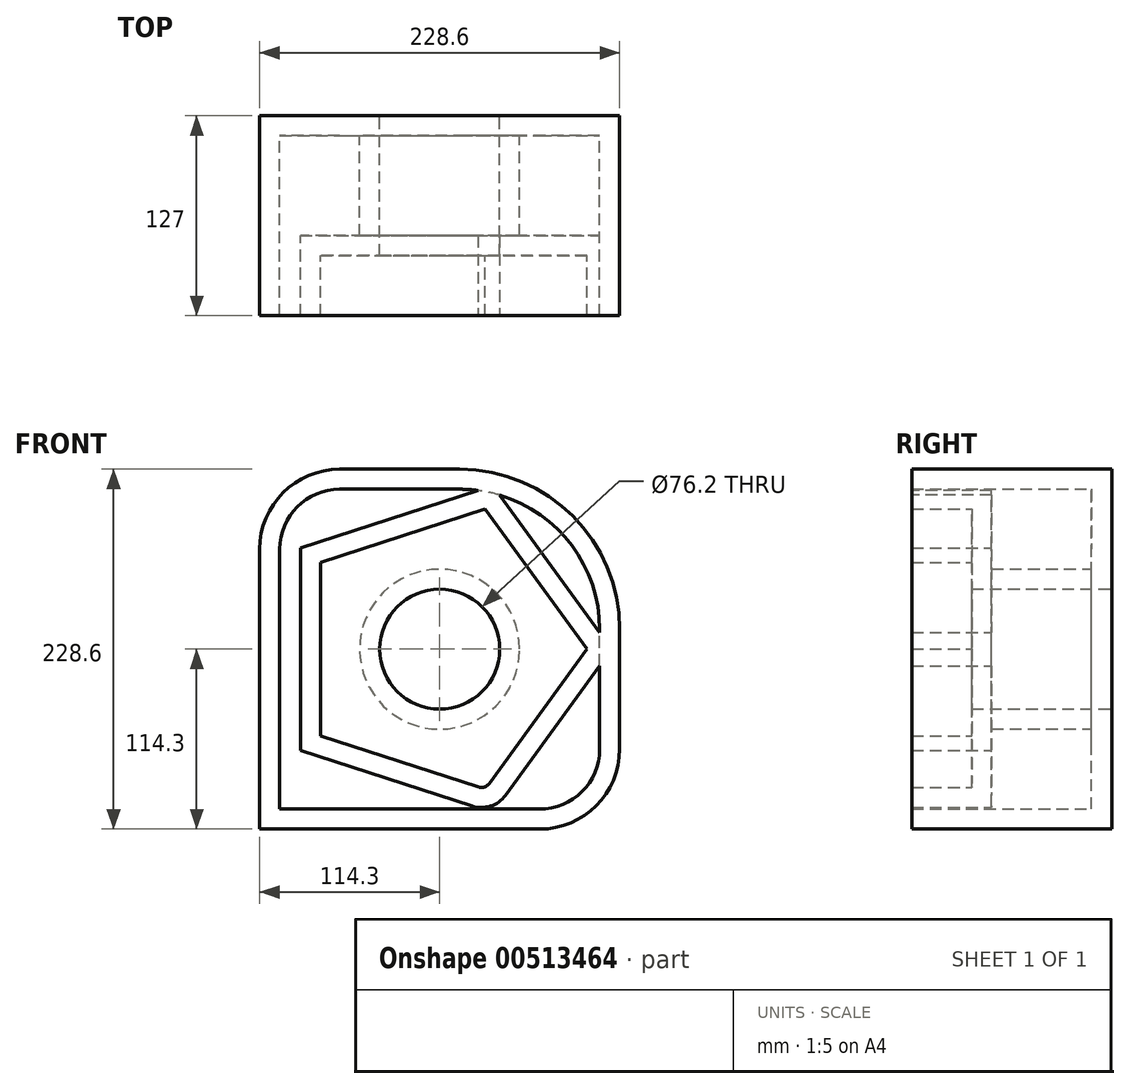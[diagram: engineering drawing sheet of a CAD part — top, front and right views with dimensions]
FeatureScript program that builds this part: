
annotation { "Feature Type Name" : "Feature", "Feature Type Description" : "" }
export const myFeature = defineFeature(function(context is Context, id is Id, definition is map)
    precondition{}
    {
        {
            var Q0;
            Q0=qCreatedBy(makeId("Front.planeOp"),FACE);
            var sketch = newSketch(context, id + "F0", { "sketchPlane" : qUnion([Q0])});
            skCircle(sketch, "E0.cCircle", {"center": v(0, 0) * mm, "radius": 75.71 * mm, "construction": true});
            skLineSegment(sketch, "E0.0", {"start": v(-75.71, -55) * mm, "end": v(-75.71, 55) * mm});
            skLineSegment(sketch, "E0.1", {"start": v(-75.71, 55) * mm, "end": v(28.92, 89) * mm});
            skLineSegment(sketch, "E0.2", {"start": v(28.92, 89) * mm, "end": v(93.59, 0) * mm});
            skLineSegment(sketch, "E0.3", {"start": v(93.59, 0) * mm, "end": v(31.63, -85.27) * mm});
            skLineSegment(sketch, "E0.4", {"start": v(24.53, -87.58) * mm, "end": v(-75.71, -55) * mm});
            skPoint(sketch, "E0.0.midPoint", {"position": v(-75.71, 0) * mm});
            skCircle(sketch, "E1", {"center": v(0, 0) * mm, "radius": 38.1 * mm});
            skPoint(sketch, "E2.visualSharp", {"position": v(28.92, -89) * mm});
            skArc(sketch, "E2.filletArc", {"start": v(24.53, -87.58) * mm, "mid": v(28.46, -87.58) * mm, "end": v(31.63, -85.27) * mm});
            skLineSegment(sketch, "E3.bottom", {"start": v(-114.3, -114.3) * mm, "end": v(63.5, -114.3) * mm});
            skLineSegment(sketch, "E3.top", {"start": v(-63.5, 114.3) * mm, "end": v(114.3, 114.3) * mm});
            skLineSegment(sketch, "E3.left", {"start": v(-114.3, -114.3) * mm, "end": v(-114.3, 63.5) * mm});
            skLineSegment(sketch, "E3.right", {"start": v(114.3, -63.5) * mm, "end": v(114.3, 114.3) * mm});
            skPoint(sketch, "E4.visualSharp", {"position": v(-114.3, 114.3) * mm});
            skArc(sketch, "E4.filletArc", {"start": v(-63.5, 114.3) * mm, "mid": v(-99.42, 99.42) * mm, "end": v(-114.3, 63.5) * mm});
            skPoint(sketch, "E5.visualSharp", {"position": v(114.3, -114.3) * mm});
            skArc(sketch, "E5.filletArc", {"start": v(63.5, -114.3) * mm, "mid": v(99.42, -99.42) * mm, "end": v(114.3, -63.5) * mm});
            skSolve(sketch);
        }
        {
            var Q0;
            Q0=makeQuery(id+"F0.imprint","IMPRINT",FACE,{"disambiguationData":[TD([[makeQuery(id+"F0.imprint","IMPRINT",EDGE,{"derivedFrom":sQuery(id+"F0.wireOp",EDGE,"E0.0")}),1.0]])]});
            extrude(context, id + "F1", {"entities" : qUnion([Q0]), "depth" : 127 * mm});
        }
        {
            var Q0;
            Q0 = qSketchRegion(id + "F0", true);
            var Q1;
            Q1=makeQuery(id+"F0.imprint","IMPRINT",FACE,{"disambiguationData":[TD([[makeQuery(id+"F0.imprint","IMPRINT",EDGE,{"derivedFrom":sQuery(id+"F0.wireOp",EDGE,"E0.0")}),-1.0]])]});
            extrude(context, id + "F2", {"entities" : qUnion([Q0, Q1]), "operationType" : NewBodyOperationType.ADD, "depth" : 88.9 * mm});
        }
        {
            var Q0;
            Q0=makeQuery(id+"F1.opExtrude","SWEPT_EDGE",EDGE,{"disambiguationData":[OSD([sQuery(id+"F0.wireOp",EDGE,"E3.top"),sQuery(id+"F0.wireOp",EDGE,"E3.right")])]});
            fillet(context, id + "F3", {"entities" : qUnion([Q0]), "radius" : 101.6 * mm, "tangentPropagation" : true, "allowEdgeOverflow" : false});
        }
        {
            var Q0;
            Q0=makeQuery(id+"F1.opExtrude","CAP_FACE",FACE,{"disambiguationData":[OSD([sQuery(id+"F0.wireOp",EDGE,"E0.0"),sQuery(id+"F0.wireOp",EDGE,"E0.1"),sQuery(id+"F0.wireOp",EDGE,"E0.2"),sQuery(id+"F0.wireOp",EDGE,"E0.3"),sQuery(id+"F0.wireOp",EDGE,"E0.4"),sQuery(id+"F0.wireOp",EDGE,"E2.filletArc"),sQuery(id+"F0.wireOp",EDGE,"E3.bottom"),sQuery(id+"F0.wireOp",EDGE,"E3.top"),sQuery(id+"F0.wireOp",EDGE,"E3.left"),sQuery(id+"F0.wireOp",EDGE,"E3.right"),sQuery(id+"F0.wireOp",EDGE,"E4.filletArc"),sQuery(id+"F0.wireOp",EDGE,"E5.filletArc")])],"isStart":false});
            shell(context, id + "F4", {"entities" : qUnion([Q0]), "thickness" : 12.7 * mm});
        }
    });
